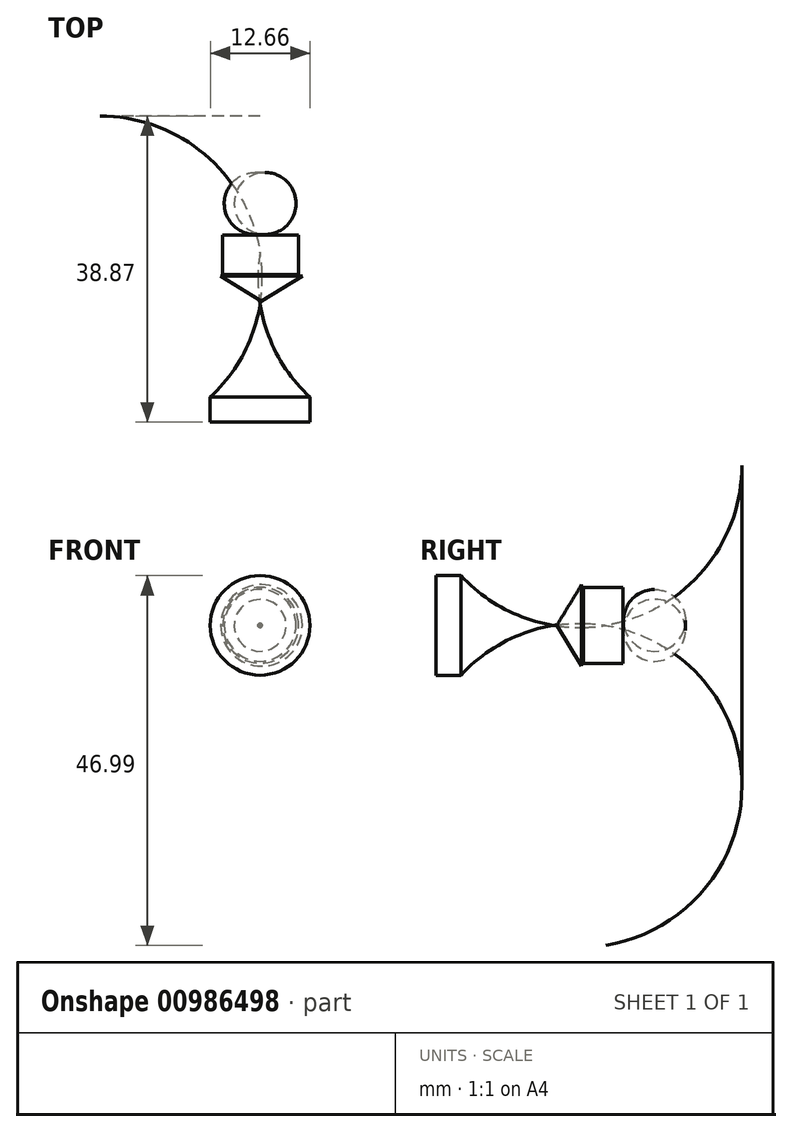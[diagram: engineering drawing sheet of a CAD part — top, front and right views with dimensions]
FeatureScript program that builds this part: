
annotation { "Feature Type Name" : "Feature", "Feature Type Description" : "" }
export const myFeature = defineFeature(function(context is Context, id is Id, definition is map)
    precondition{}
    {
        {
            var Q0;
            Q0=qCreatedBy(makeId("Top.planeOp"),FACE);
            var sketch = newSketch(context, id + "F0", { "sketchPlane" : qUnion([Q0])});
            skLineSegment(sketch, "E0", {"start": v(22.7, -26.72) * mm, "end": v(29.03, -26.72) * mm});
            skLineSegment(sketch, "E1", {"start": v(29.03, -26.72) * mm, "end": v(29.03, -23.56) * mm});
            skArc(sketch, "E2", {"start": v(22.7, -5.14) * mm, "mid": v(23.55, -15.14) * mm, "end": v(29.03, -23.56) * mm});
            skArc(sketch, "E3", {"start": v(22.7, -2.84) * mm, "mid": v(27.26, 1.05) * mm, "end": v(22.7, 4.93) * mm});
            skLineSegment(sketch, "E4", {"start": v(22.7, -26.72) * mm, "end": v(22.7, -5.14) * mm});
            skLineSegment(sketch, "E5", {"start": v(22.7, 4.93) * mm, "end": v(22.7, -2.84) * mm});
            skSolve(sketch);
        }
        {
            var Q0;
            Q0 = qSketchRegion(id + "F0", true);
            var Q1;
            Q1=sQuery(id+"F0.wireOp",EDGE,"E4");
            revolve(context, id + "F1", {"surfaceOperationType" : NewSurfaceOperationType.NEW, "entities" : qUnion([Q0]), "axis" : qUnion([Q1]), "revolveType" : RevolveType.FULL});
        }
        {
            var Q0;
            Q0=qCreatedBy(makeId("Top.planeOp"),FACE);
            var sketch = newSketch(context, id + "F2", { "sketchPlane" : qUnion([Q0])});
            skLineSegment(sketch, "E6", {"start": v(22.88, -11.37) * mm, "end": v(28.06, -8.2) * mm});
            skLineSegment(sketch, "E7", {"start": v(28.06, -8.2) * mm, "end": v(22.88, -8.2) * mm});
            skLineSegment(sketch, "E8", {"start": v(22.88, -8.2) * mm, "end": v(22.88, -3.6) * mm});
            skLineSegment(sketch, "E9", {"start": v(22.88, -3.6) * mm, "end": v(22.88, -11.37) * mm});
            skSolve(sketch);
        }
        {
            var Q0;
            {var subQ0=sQuery(id+"F2.wireOp",EDGE,"E6");Q0=makeQuery(id+"F2.imprint","IMPRINT",FACE,{"disambiguationData":[TD([[makeQuery(id+"F2.imprint","IMPRINT",EDGE,{"derivedFrom":subQ0}),1.0]])]});}
            var Q1;
            Q1=sQuery(id+"F2.wireOp",EDGE,"E9");
            revolve(context, id + "F3", {"operationType" : NewBodyOperationType.ADD, "surfaceOperationType" : NewSurfaceOperationType.NEW, "entities" : qUnion([Q0]), "axis" : qUnion([Q1]), "revolveType" : RevolveType.FULL});
        }
        {
            var Q0;
            Q0=qCreatedBy(makeId("Top.planeOp"),FACE);
            var sketch = newSketch(context, id + "F4", { "sketchPlane" : qUnion([Q0])});
            skLineSegment(sketch, "E10.bottom", {"start": v(17.93, -7.97) * mm, "end": v(22.75, -7.97) * mm});
            skLineSegment(sketch, "E10.top", {"start": v(17.93, -2.94) * mm, "end": v(22.75, -2.94) * mm});
            skLineSegment(sketch, "E10.left", {"start": v(17.93, -7.97) * mm, "end": v(17.93, -2.94) * mm});
            skLineSegment(sketch, "E10.right", {"start": v(22.75, -7.97) * mm, "end": v(22.75, -2.94) * mm});
            skSolve(sketch);
        }
        {
            var Q0;
            Q0=makeQuery(id+"F4.imprint","IMPRINT",FACE,{"disambiguationData":[TD([[makeQuery(id+"F4.imprint","IMPRINT",EDGE,{"derivedFrom":sQuery(id+"F4.wireOp",EDGE,"E10.bottom")}),1.0]])]});
            var Q1;
            Q1=sQuery(id+"F4.wireOp",EDGE,"E10.right");
            revolve(context, id + "F5", {"operationType" : NewBodyOperationType.ADD, "surfaceOperationType" : NewSurfaceOperationType.NEW, "entities" : qUnion([Q0]), "axis" : qUnion([Q1]), "revolveType" : RevolveType.FULL});
        }
    });
